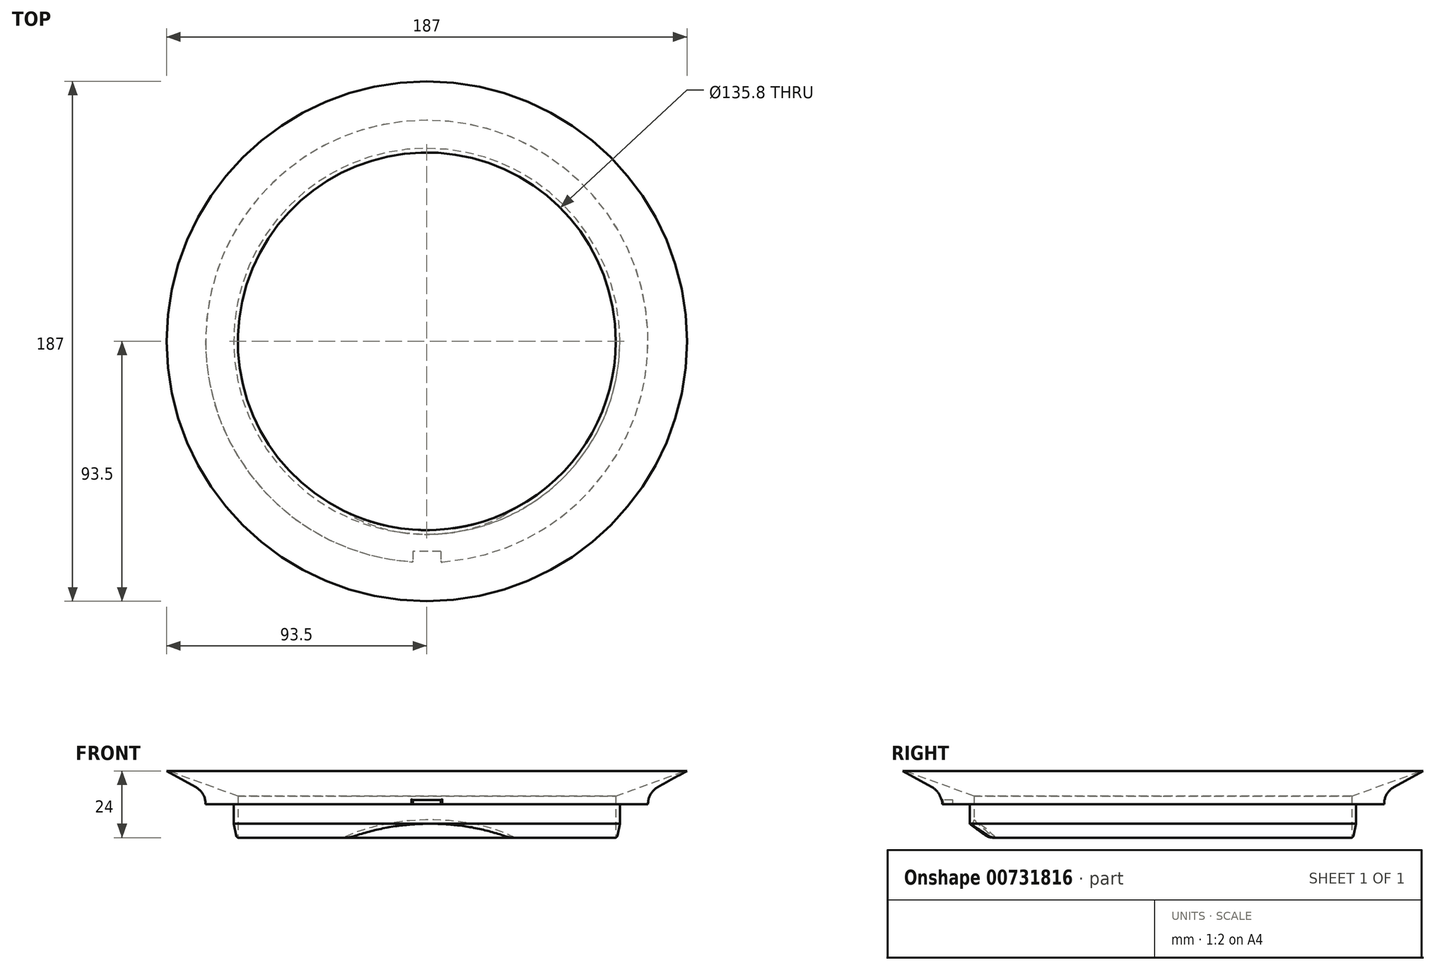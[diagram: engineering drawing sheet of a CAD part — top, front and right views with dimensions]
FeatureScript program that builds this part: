
annotation { "Feature Type Name" : "Feature", "Feature Type Description" : "" }
export const myFeature = defineFeature(function(context is Context, id is Id, definition is map)
    precondition{}
    {
        {
            var Q0;
            Q0=qCreatedBy(makeId("Top.planeOp"),FACE);
            var sketch = newSketch(context, id + "F0", { "sketchPlane" : qUnion([Q0])});
            skCircle(sketch, "E0", {"center": v(0, 0) * mm, "radius": 69.5 * mm, "construction": true});
            skCircle(sketch, "E1", {"center": v(0, 0) * mm, "radius": 68.5 * mm, "construction": true});
            skCircle(sketch, "E2", {"center": v(0, 0) * mm, "radius": 74.5 * mm, "construction": true});
            skCircle(sketch, "E3", {"center": v(0, 0) * mm, "radius": 75.5 * mm, "construction": true});
            skCircle(sketch, "E4", {"center": v(0, 0) * mm, "radius": 93.5 * mm, "construction": true});
            skSolve(sketch);
        }
        {
            var Q0;
            Q0=qCreatedBy(makeId("Top.planeOp"),FACE);
            var sketch = newSketch(context, id + "F1", { "sketchPlane" : qUnion([Q0])});
            skCircle(sketch, "E5", {"center": v(0, 0) * mm, "radius": 69.4 * mm});
            skCircle(sketch, "E6", {"center": v(0, 0) * mm, "radius": 67.9 * mm});
            skSolve(sketch);
        }
        {
            var Q0;
            Q0=makeQuery(id+"F1.imprint","IMPRINT",FACE,{"disambiguationData":[TD([[makeQuery(id+"F1.imprint","IMPRINT",EDGE,{"derivedFrom":sQuery(id+"F1.wireOp",EDGE,"E5")}),1.0]])]});
            extrude(context, id + "F2", {"entities" : qUnion([Q0]), "oppositeDirection" : true, "depth" : 12 * mm, "offsetDistance" : 25 * mm});
        }
        {
            var Q0;
            Q0=qCreatedBy(makeId("Top.planeOp"),FACE);
            var sketch = newSketch(context, id + "F3", { "sketchPlane" : qUnion([Q0])});
            skCircle(sketch, "E7", {"center": v(0, 0) * mm, "radius": 67.9 * mm});
            skCircle(sketch, "E8", {"center": v(0, 0) * mm, "radius": 79.5 * mm});
            skSolve(sketch);
        }
        {
            var Q0;
            Q0=makeQuery(id+"F3.imprint","IMPRINT",FACE,{"disambiguationData":[TD([[makeQuery(id+"F3.imprint","IMPRINT",EDGE,{"derivedFrom":sQuery(id+"F3.wireOp",EDGE,"E7")}),-1.0]])]});
            extrude(context, id + "F4", {"entities" : qUnion([Q0]), "depth" : 2 * mm, "offsetDistance" : 25 * mm});
        }
        {
            var Q0;
            Q0=makeQuery(id+"F4.opExtrude","CAP_FACE",FACE,{"disambiguationData":[OSD([sQuery(id+"F3.wireOp",EDGE,"E7"),sQuery(id+"F3.wireOp",EDGE,"E8")])],"isStart":false});
            var sketch = newSketch(context, id + "F5", { "sketchPlane" : qUnion([Q0])});
            skCircle(sketch, "E9", {"center": v(0, 0) * mm, "radius": 67.9 * mm});
            skCircle(sketch, "E10", {"center": v(0, 0) * mm, "radius": 93.5 * mm});
            skSolve(sketch);
        }
        {
            var Q0;
            Q0 = qSketchRegion(id + "F5", true);
            extrude(context, id + "F6", {"entities" : qUnion([Q0]), "operationType" : NewBodyOperationType.ADD, "depth" : 10 * mm, "offsetDistance" : 25 * mm});
        }
        {
            var Q0;
            Q0=makeQuery(id+"F6.opExtrude","CAP_EDGE",EDGE,{"disambiguationData":[OSD([sQuery(id+"F5.wireOp",EDGE,"E9")])],"isStart":false});
            chamfer(context, id + "F7", {"entities" : qUnion([Q0]), "chamferType" : ChamferType.TWO_OFFSETS, "width1" : 9.1 * mm, "oppositeDirection" : false, "width2" : 25 * mm, "tangentPropagation" : true});
        }
        {
            var Q0;
            Q0=makeQuery(id+"F6.opExtrude","CAP_EDGE",EDGE,{"disambiguationData":[OSD([sQuery(id+"F5.wireOp",EDGE,"E10")])],"isStart":true});
            chamfer(context, id + "F8", {"entities" : qUnion([Q0]), "chamferType" : ChamferType.TWO_OFFSETS, "width1" : 10 * mm, "oppositeDirection" : false, "width2" : 18 * mm, "tangentPropagation" : true});
        }
        {
            var Q0;
            Q0=makeQuery(id+"F4.opExtrude","SWEPT_BODY",BODY,{"disambiguationData":[OSD([sQuery(id+"F3.wireOp",EDGE,"E7"),sQuery(id+"F3.wireOp",EDGE,"E8")])]});
            var Q1;
            Q1=makeQuery(id+"F2.opExtrude","SWEPT_BODY",BODY,{"disambiguationData":[OSD([sQuery(id+"F1.wireOp",EDGE,"E5"),sQuery(id+"F1.wireOp",EDGE,"E6")])]});
            booleanBodies(context, id + "F9", {"operationType" : BooleanOperationType.UNION, "tools" : qUnion([Q0, Q1])});
        }
        {
            var Q0;
            Q0=makeQuery(id+"F8.opChamfer","BLEND_EDGE",EDGE,{"blendedFrom":[makeQuery(id+"F6.opExtrude","CAP_EDGE",EDGE,{"disambiguationData":[OSD([sQuery(id+"F5.wireOp",EDGE,"E10")])],"isStart":true}),makeQuery(id+"F4.opExtrude","SWEPT_FACE",FACE,{"disambiguationData":[OSD([sQuery(id+"F3.wireOp",EDGE,"E8")])]})],"blendedInto":[makeQuery(id+"F4.opExtrude","SWEPT_FACE",FACE,{"disambiguationData":[OSD([sQuery(id+"F3.wireOp",EDGE,"E8")])]})]});
            fillet(context, id + "F10", {"entities" : qUnion([Q0]), "radius" : 7 * mm, "tangentPropagation" : true, "allowEdgeOverflow" : false});
        }
        {
            var Q0;
            Q0=makeQuery(id+"F2.opExtrude","CAP_EDGE",EDGE,{"disambiguationData":[OSD([sQuery(id+"F1.wireOp",EDGE,"E5")])],"isStart":false});
            chamfer(context, id + "F11", {"entities" : qUnion([Q0]), "chamferType" : ChamferType.TWO_OFFSETS, "width1" : 5 * mm, "oppositeDirection" : false, "width2" : 1 * mm, "tangentPropagation" : true});
        }
        {
            var Q0;
            {var subQ0=sQuery(id+"F1.wireOp",EDGE,"E5");Q0=makeQuery(id+"F11.opChamfer","BLEND_EDGE",EDGE,{"blendedFrom":[makeQuery(id+"F2.opExtrude","CAP_EDGE",EDGE,{"disambiguationData":[OSD([subQ0])],"isStart":false}),makeQuery(id+"F2.opExtrude","CAP_FACE",FACE,{"disambiguationData":[OSD([subQ0,sQuery(id+"F1.wireOp",EDGE,"E6")])],"isStart":false})],"blendedInto":[makeQuery(id+"F2.opExtrude","CAP_FACE",FACE,{"disambiguationData":[OSD([subQ0,sQuery(id+"F1.wireOp",EDGE,"E6")])],"isStart":false})]});}
            fillet(context, id + "F12", {"entities" : qUnion([Q0]), "radius" : 1 * mm, "tangentPropagation" : true, "allowEdgeOverflow" : false});
        }
        {
            var Q0;
            {var subQ0=sQuery(id+"F5.wireOp",EDGE,"E9");Q0=makeQuery(id+"F7.opChamfer","BLEND_EDGE",EDGE,{"blendedFrom":[makeQuery(id+"F6.opExtrude","CAP_EDGE",EDGE,{"disambiguationData":[OSD([subQ0])],"isStart":false}),makeQuery(id+"F6.opExtrude","CAP_FACE",FACE,{"disambiguationData":[OSD([subQ0,sQuery(id+"F5.wireOp",EDGE,"E10")])],"isStart":false})],"blendedInto":[makeQuery(id+"F6.opExtrude","CAP_FACE",FACE,{"disambiguationData":[OSD([subQ0,sQuery(id+"F5.wireOp",EDGE,"E10")])],"isStart":false})]});}
            fillet(context, id + "F13", {"entities" : qUnion([Q0]), "radius" : 6 * mm, "tangentPropagation" : true, "allowEdgeOverflow" : false});
        }
        {
            var Q0;
            Q0=qCreatedBy(makeId("Front.planeOp"),FACE);
            var sketch = newSketch(context, id + "F14", { "sketchPlane" : qUnion([Q0])});
            skCircle(sketch, "E11", {"center": v(0, -29.5) * mm, "radius": 22.5 * mm});
            skEllipse(sketch, "E12", {"center": v(0, -29.5) * mm, "majorRadius": 44.58 * mm, "minorRadius": 22.5 * mm, "majorAxis": v(-1, -0.02)});
            skPoint(sketch, "E13", {"position": v(0, -7) * mm});
            skSolve(sketch);
        }
        {
            var Q0;
            Q0=makeQuery(id+"F14.imprint","IMPRINT",FACE,{"disambiguationData":[TD([[makeQuery(id+"F14.imprint","IMPRINT",EDGE,{"derivedFrom":sQuery(id+"F14.wireOp",EDGE,"E11")}),1.0]])]});
            extrude(context, id + "F15", {"entities" : qUnion([Q0]), "operationType" : NewBodyOperationType.REMOVE, "depth" : 100 * mm, "offsetDistance" : 25 * mm});
        }
        {
            var Q0;
            Q0=makeQuery(id+"F15.boolean.opBoolean","INTERSECT",EDGE,{"derivedFrom":[makeQuery(id+"F9.opBoolean","MERGE",FACE,{"derivedFrom":[makeQuery(id+"F2.opExtrude","SWEPT_FACE",FACE,{"disambiguationData":[OSD([sQuery(id+"F1.wireOp",EDGE,"E6")])]}),makeQuery(id+"F6.boolean.opBoolean","MERGE",FACE,{"derivedFrom":[makeQuery(id+"F4.opExtrude","SWEPT_FACE",FACE,{"disambiguationData":[OSD([sQuery(id+"F3.wireOp",EDGE,"E7")])]}),makeQuery(id+"F6.opExtrude","SWEPT_FACE",FACE,{"disambiguationData":[OSD([sQuery(id+"F5.wireOp",EDGE,"E9")])]})]})]}),makeQuery(id+"F15.opExtrude","SWEPT_FACE",FACE,{"disambiguationData":[OSD([sQuery(id+"F14.wireOp",EDGE,"E11")])]})]});
            fillet(context, id + "F16", {"entities" : qUnion([Q0]), "radius" : 8.8 * mm, "tangentPropagation" : true, "allowEdgeOverflow" : false});
        }
        {
            var Q0;
            Q0 = qSketchRegion(id + "F14", true);
            extrude(context, id + "F17", {"entities" : qUnion([Q0]), "operationType" : NewBodyOperationType.REMOVE, "depth" : 100 * mm, "offsetDistance" : 25 * mm});
        }
        {
            var Q0;
            {var subQ0=sQuery(id+"F14.wireOp",EDGE,"E12");var subQ1=sQuery(id+"F14.wireOp",EDGE,"E11");Q0=makeQuery(id+"F17.boolean.opBoolean","INTERSECT",EDGE,{"derivedFrom":[makeQuery(id+"F9.opBoolean","MERGE",FACE,{"derivedFrom":[makeQuery(id+"F2.opExtrude","SWEPT_FACE",FACE,{"disambiguationData":[OSD([sQuery(id+"F1.wireOp",EDGE,"E6")])]}),makeQuery(id+"F6.boolean.opBoolean","MERGE",FACE,{"derivedFrom":[makeQuery(id+"F4.opExtrude","SWEPT_FACE",FACE,{"disambiguationData":[OSD([sQuery(id+"F3.wireOp",EDGE,"E7")])]}),makeQuery(id+"F6.opExtrude","SWEPT_FACE",FACE,{"disambiguationData":[OSD([sQuery(id+"F5.wireOp",EDGE,"E9")])]})]})]}),makeQuery(id+"F17.opExtrude","SWEPT_FACE",FACE,{"disambiguationData":[OSD([subQ0]),TDD([makeQuery(id+"F14.imprint","IMPRINT",EDGE,{"disambiguationData":[TD([[makeQuery(id+"F14.imprint","INTERSECT",VERTEX,{"disambiguationData":[OD(0.0)],"derivedFrom":[subQ1,subQ0]}),-1.0]])],"derivedFrom":subQ0})])]})]});}
            fillet(context, id + "F18", {"entities" : qUnion([Q0]), "radius" : 1.4 * mm, "tangentPropagation" : true, "allowEdgeOverflow" : false});
        }
        {
            var Q0;
            Q0=qCreatedBy(makeId("Front.planeOp"),FACE);
            cPlane(context, id + "F19", {"entities" : qUnion([Q0]), "cplaneType" : CPlaneType.OFFSET, "offset" : 79.5 * mm, "width" : 150 * mm, "height" : 150 * mm});
        }
        {
            var Q0;
            Q0=qCreatedBy(id+"F19.planeOp",FACE);
            var sketch = newSketch(context, id + "F20", { "sketchPlane" : qUnion([Q0])});
            skLineSegment(sketch, "E14.bottom", {"start": v(5, 0) * mm, "end": v(-5, 0) * mm});
            skLineSegment(sketch, "E14.top", {"start": v(5, 1.5) * mm, "end": v(-5, 1.5) * mm});
            skLineSegment(sketch, "E14.left", {"start": v(5, -0.5) * mm, "end": v(5, 1.5) * mm});
            skLineSegment(sketch, "E14.right", {"start": v(-5, 0) * mm, "end": v(-5, 1.5) * mm});
            skPoint(sketch, "E14.middle", {"position": v(0, 0.75) * mm});
            skSolve(sketch);
        }
        {
            var Q0;
            Q0 = qSketchRegion(id + "F20", true);
            extrude(context, id + "F21", {"entities" : qUnion([Q0]), "operationType" : NewBodyOperationType.REMOVE, "endBound" : BoundingType.SYMMETRIC, "oppositeDirection" : true, "depth" : 8 * mm, "offsetDistance" : 25 * mm});
        }
        {
            var Q0;
            Q0=makeQuery(id+"F21.boolean.opBoolean","INTERSECT",EDGE,{"derivedFrom":[makeQuery(id+"F10.opFillet","BLEND_FACE",FACE,{"disambiguationData":[OSD([sQuery(id+"F3.wireOp",EDGE,"E8"),sQuery(id+"F5.wireOp",EDGE,"E10")])]}),makeQuery(id+"F21.opExtrude","SWEPT_FACE",FACE,{"disambiguationData":[OSD([sQuery(id+"F20.wireOp",EDGE,"E14.top")])]})]});
            var Q1;
            Q1=makeQuery(id+"F21.boolean.opBoolean","INTERSECT",EDGE,{"derivedFrom":[makeQuery(id+"F10.opFillet","BLEND_FACE",FACE,{"disambiguationData":[OSD([sQuery(id+"F3.wireOp",EDGE,"E8"),sQuery(id+"F5.wireOp",EDGE,"E10")])]}),makeQuery(id+"F21.opExtrude","SWEPT_FACE",FACE,{"disambiguationData":[OSD([sQuery(id+"F20.wireOp",EDGE,"E14.right")])]})]});
            var Q2;
            Q2=makeQuery(id+"F21.boolean.opBoolean","INTERSECT",EDGE,{"derivedFrom":[makeQuery(id+"F10.opFillet","BLEND_FACE",FACE,{"disambiguationData":[OSD([sQuery(id+"F3.wireOp",EDGE,"E8"),sQuery(id+"F5.wireOp",EDGE,"E10")])]}),makeQuery(id+"F21.opExtrude","SWEPT_FACE",FACE,{"disambiguationData":[OSD([sQuery(id+"F20.wireOp",EDGE,"E14.left")])]})]});
            var Q3;
            Q3=makeQuery(id+"F10.opFillet","BLEND_FACE",FACE,{"disambiguationData":[OSD([sQuery(id+"F3.wireOp",EDGE,"E8"),sQuery(id+"F5.wireOp",EDGE,"E10")])]});
            fillet(context, id + "F22", {"entities" : qUnion([Q0, Q1, Q2, Q3]), "radius" : 0.5 * mm, "tangentPropagation" : true, "allowEdgeOverflow" : false});
        }
    });
